# Revit family: PRD_AR_TltRllHldrs_RODANDoubleToiletRollHolder_RODX672E
name_source: partatom
category: Specialty Equipment
revit_build: Autodesk Revit 2018 (Build: 20190510_1515(x64)
units: mm (PartAtom-declared; Revit-internal decimal feet)

## family parameters
Cut with Voids When Loaded = Yes
Host = Face
OmniClass Number = 23.40.20.21.21
OmniClass Title = Toilet Paper Dispensers
Part Type = Normal
Room Calculation Point = No
Round Connector Dimension = Use Diameter
Shared = No

## types (1)
- RODX672E
    AssetType = Fixed
    BIMObjectName = PRD_AR_ToiletRollHolders_RODANDoubleToiletRollHolder_RODX672E
    Category = Pr_40_20_76_88, Toilet roll holders
    Default Elevation = 600 mm
    Description = Double toilet roll holder with spindle system for recessed mounting, stainless steel, surface satin finished, material thickness 0.8 mm, folded front cover, cylinder lock with KWC standard key, for 2 rolls with max. diameter 120 mm, second roll will be released after consumption of first roll, reserve roll not visible, includes stainless steel screws and dowels.
    DurationUnit = year
    Features = stainless steel, surface satin finished
    FillingQuantity = 2
    FillingQuantityUom = Rolls
    Finish = satin finished
    GrossWeight = 2.75 kg
    HolderMaterial = PRD_AR_StainlessSteel_SatinFinished
    IfcExportAs = IfcFurnitureType
    IfcExportType = USERDEFINED
    IntegralAccessories = incl. stainless steel screws and dowels
    IsBuiltIn = TRUE
    Lock = Key-lock
    MainColor = stainless steel
    Manufacturer = KWC Group AG
    ManufacturerName = KWC Group AG
    ManufacturerURL = www.kwc.com
    Material = stainless steel
    MaterialCode = 1.4301
    MaterialThickness = 0.80 mm
    MaximumDepthDiameterOfConsumable = 115.00 mm
    MaximumWidthOfConsumable = 115.00 mm
    Model = RODX672E
    ModelNumber = 2000090073
    ModelReference = RODX672E
    NBSDescription = Toilet roll holders
    NBSReference = 45-35-72/368
    Name = Double toilet roll holder RODX672E
    NetWeight = 2.55 kg
    NominalDepth = 138 mm  [stored 0.452756 ft]
    NominalHeight = 341 mm
    NominalWidth = 184 mm  [stored 0.603675 ft]
    Offset = 0 mm  [stored 0 ft]
    ProductInformation = https://pim.kwc.com
    Size = 184 x 341 x 138 mm
    Spindle = Yes
    Style = Roll holder
    ToiletRollMaterial = PRD_AR_ToiletRoll
    TypeOfFixing = Screw
    TypeOfMounting = Recessed mounting
    URL = www.kwc.com
    Uniclass2015Code = Pr_40_20_76_88
    Uniclass2015Title = Toilet roll holders
    Uniclass2015Version = Products v1.17
    Version = 1
    WarrantyDurationUnit = year

note: [stored X ft] marks values corroborated as IEEE doubles in the binary element streams (Revit-internal decimal feet)

## geometry (parser evidence)
native form markers: Sweep x5
no freeform markers — native parametric forms only
